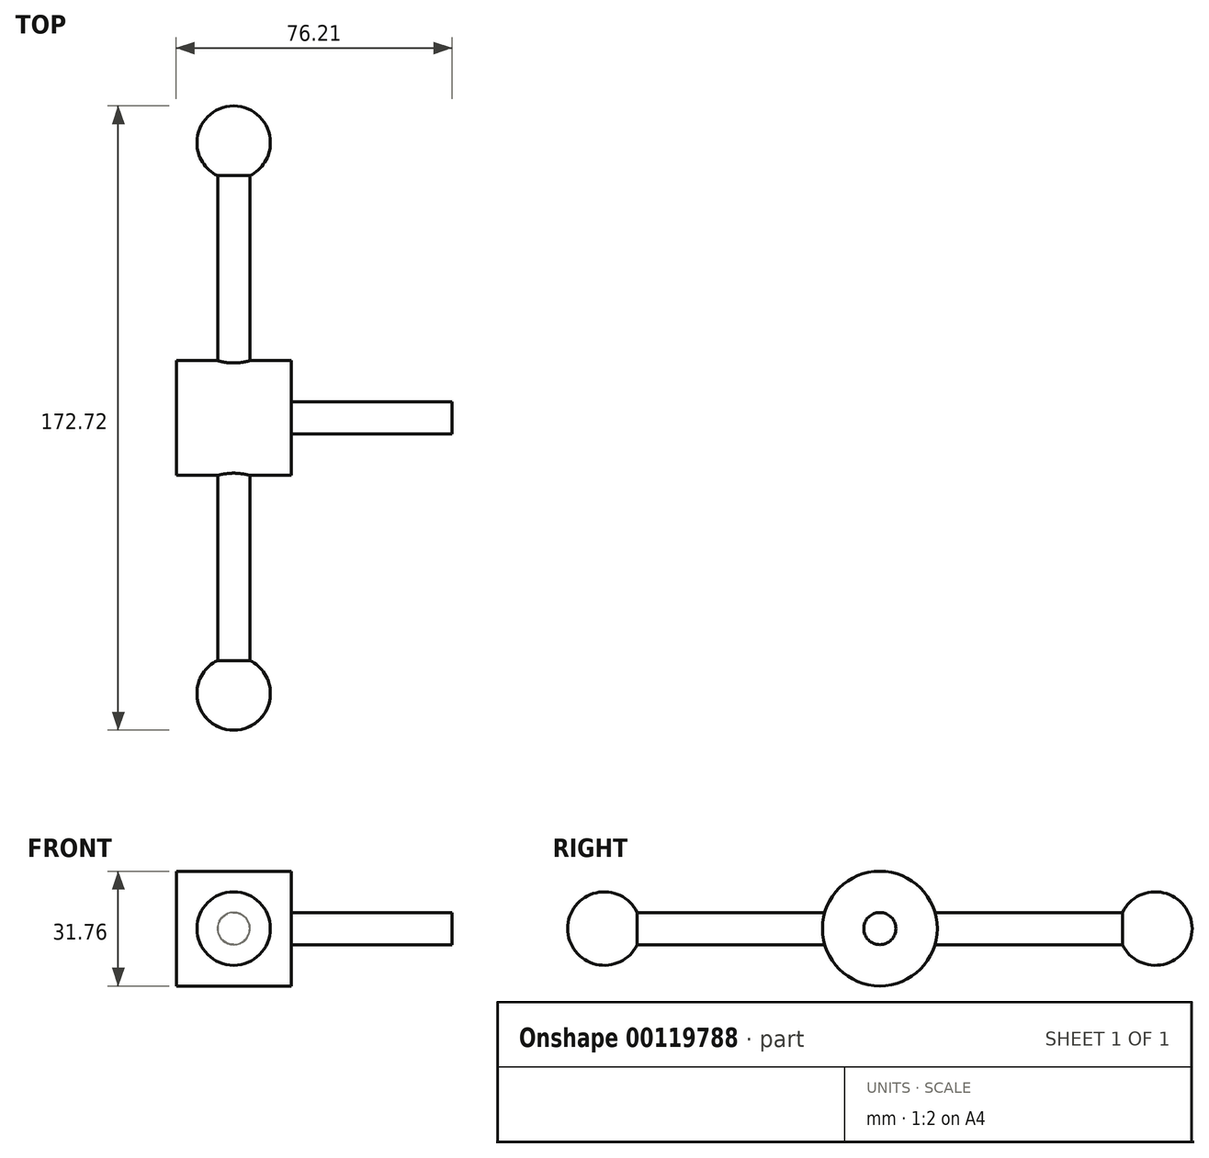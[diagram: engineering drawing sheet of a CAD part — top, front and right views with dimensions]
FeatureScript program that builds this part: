
annotation { "Feature Type Name" : "Feature", "Feature Type Description" : "" }
export const myFeature = defineFeature(function(context is Context, id is Id, definition is map)
    precondition{}
    {
        {
            var Q0;
            Q0=qCreatedBy(makeId("Right.planeOp"),FACE);
            var sketch = newSketch(context, id + "F0", { "sketchPlane" : qUnion([Q0])});
            skCircle(sketch, "E0", {"center": v(0, 0) * mm, "radius": 15.88 * mm});
            skSolve(sketch);
        }
        {
            var Q0;
            Q0 = qSketchRegion(id + "F0", true);
            extrude(context, id + "F1", {"entities" : qUnion([Q0]), "endBound" : BoundingType.SYMMETRIC, "depth" : 31.75 * mm});
        }
        {
            var Q0;
            Q0=makeQuery(id+"F1.opExtrude","CAP_FACE",FACE,{"disambiguationData":[OSD([sQuery(id+"F0.wireOp",EDGE,"E0")])],"isStart":false});
            var sketch = newSketch(context, id + "F2", { "sketchPlane" : qUnion([Q0])});
            skCircle(sketch, "E1", {"center": v(0, 0) * mm, "radius": 4.45 * mm});
            skSolve(sketch);
        }
        {
            var Q0;
            Q0 = qSketchRegion(id + "F2", true);
            extrude(context, id + "F3", {"entities" : qUnion([Q0]), "operationType" : NewBodyOperationType.ADD, "depth" : 44.45 * mm});
        }
        {
            var Q0;
            Q0=qCreatedBy(makeId("Front.planeOp"),FACE);
            var sketch = newSketch(context, id + "F4", { "sketchPlane" : qUnion([Q0])});
            skCircle(sketch, "E2", {"center": v(0, 0) * mm, "radius": 4.45 * mm});
            skSolve(sketch);
        }
        {
            var Q0;
            Q0 = qSketchRegion(id + "F4", true);
            extrude(context, id + "F5", {"entities" : qUnion([Q0]), "operationType" : NewBodyOperationType.ADD, "endBound" : BoundingType.SYMMETRIC, "depth" : 152.4 * mm});
        }
        {
            var Q0;
            Q0=qCreatedBy(makeId("Top.planeOp"),FACE);
            var sketch = newSketch(context, id + "F6", { "sketchPlane" : qUnion([Q0])});
            skLineSegment(sketch, "E3", {"start": v(-4.45, 15.87) * mm, "end": v(-4.45, 76.2) * mm});
            skLineSegment(sketch, "E4.0", {"start": v(4.45, 76.2) * mm, "end": v(-4.45, 76.2) * mm});
            skLineSegment(sketch, "E5", {"start": v(4.45, 76.2) * mm, "end": v(4.45, 15.87) * mm});
            skLineSegment(sketch, "E6", {"start": v(0, 66.68) * mm, "end": v(0, 100.16) * mm, "construction": true});
            skLineSegment(sketch, "E7", {"start": v(-54.47, 76.2) * mm, "end": v(83.68, 76.2) * mm, "construction": true});
            skLineSegment(sketch, "E8", {"start": v(-9.68, 76.2) * mm, "end": v(-54.47, 76.2) * mm, "construction": true});
            skArc(sketch, "E9", {"start": v(10.16, 76.2) * mm, "mid": v(0, 86.36) * mm, "end": v(-10.16, 76.2) * mm});
            skLineSegment(sketch, "E10", {"start": v(-10.16, 76.2) * mm, "end": v(10.16, 76.2) * mm});
            skSolve(sketch);
        }
        {
            var Q0;
            {var subQ0=sQuery(id+"F6.wireOp",EDGE,"E9");Q0=makeQuery(id+"F6.imprint","IMPRINT",FACE,{"disambiguationData":[TD([[makeQuery(id+"F6.imprint","IMPRINT",EDGE,{"derivedFrom":subQ0}),1.0]])]});}
            var Q1;
            Q1=sQuery(id+"F6.wireOp",EDGE,"E7");
            revolve(context, id + "F7", {"operationType" : NewBodyOperationType.ADD, "entities" : qUnion([Q0]), "axis" : qUnion([Q1]), "revolveType" : RevolveType.FULL});
        }
        {
            var Q0;
            Q0=qCreatedBy(makeId("Top.planeOp"),FACE);
            var sketch = newSketch(context, id + "F8", { "sketchPlane" : qUnion([Q0])});
            skLineSegment(sketch, "E11", {"start": v(-30.28, -76.2) * mm, "end": v(38.67, -76.2) * mm, "construction": true});
            skLineSegment(sketch, "E12", {"start": v(0, -63.72) * mm, "end": v(0, -102.36) * mm, "construction": true});
            skArc(sketch, "E13", {"start": v(-10.16, -76.2) * mm, "mid": v(0, -86.36) * mm, "end": v(10.16, -76.2) * mm});
            skLineSegment(sketch, "E14", {"start": v(-10.16, -76.2) * mm, "end": v(10.16, -76.2) * mm});
            skSolve(sketch);
        }
        {
            var Q0;
            Q0=makeQuery(id+"F8.imprint","IMPRINT",FACE,{"disambiguationData":[TD([[makeQuery(id+"F8.imprint","IMPRINT",EDGE,{"derivedFrom":sQuery(id+"F8.wireOp",EDGE,"E13")}),1.0]])]});
            var Q1;
            Q1=sQuery(id+"F8.wireOp",EDGE,"E11");
            revolve(context, id + "F9", {"operationType" : NewBodyOperationType.ADD, "entities" : qUnion([Q0]), "axis" : qUnion([Q1]), "revolveType" : RevolveType.FULL});
        }
    });
